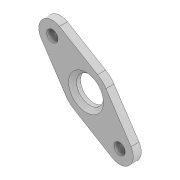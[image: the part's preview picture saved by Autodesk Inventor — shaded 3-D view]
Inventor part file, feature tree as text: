
AUTODESK INVENTOR PART (.ipt)
format: ipt  version: 2022 (Build 260153000, 153)  size: 138,752 bytes
history: native  units: mm
features: reference x6, sketch x4, extrude x3, other x2, hole x1, chamfer x1, projected_geometry x1
ambient origin geometry x8: Origin, YZ Plane, XZ Plane, XY Plane, X Axis, Y Axis, Z Axis, Center Point
bodies: Volumenkörper1 (feature_tree)
feature tree (18):
  extrude  "Extrusion1"  Depth=2.0mm
  extrude  "Extrusion2"  Depth=6.7mm
  extrude  "Extrusion3"  Depth=2.0mm TaperAngle=45.0deg
  hole  "Bohrung1"  [1 undecoded]
  chamfer  "Fase1"  [1 undecoded]
  sketch  "Skizze1"  dims[d0=2.0mm d1=0.0mm d2=2.0mm]
  reference  "Referenz1"
  reference  "Referenz2"
  reference  "Referenz3"
  sketch  "Skizze2"  dims[d3=3.0mm d4=0.0mm d5=6.7mm]
  projected_geometry  "Projizierte Kontur1"
  sketch  "Skizze3"  dims[d6=3.0mm d7=0.0mm]
  reference  "Referenz4"
  reference  "Referenz5"
  reference  "Referenz6"
  sketch  "Skizze4"  dims[d8=2.8mm d9=6.0mm d10=8.0mm d11=6.0mm d12=90.0deg d13=8.0mm d14=20.594885mm d15=1.0mm d16=2.0mm d17=45.0deg d18=0.872665mm]
  other  "Assembly_Matchboxscope_injectionmolded.iam"
  other  "IM_Matchboxscope_base:1"
note: 2 required parameter values undecoded (feature->parameter linkage not recoverable at this tier; creation-order binding heuristic only, values carry confidence <= 0.55)
